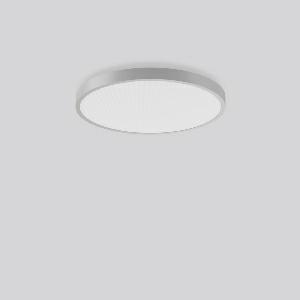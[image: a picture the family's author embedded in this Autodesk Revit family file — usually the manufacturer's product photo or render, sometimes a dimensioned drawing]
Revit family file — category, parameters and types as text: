
# Revit family: triona_round_a_312297_004_76_ec22
name_source: partatom
category: Lighting Fixtures
units: mm (PartAtom-declared; Revit-internal decimal feet)

## family parameters
Cut with Voids When Loaded = No
Host = Face
Light Source = No
Part Type = Normal
Room Calculation Point = No
Round Connector Dimension = Use Diameter
Shared = No

## types (1)
- TRIONA round A (1 x LED Modul 830, 6700 lm, 3000)
    Apparent Load = 64 VA
    CIE Flux Codes = 58 86 97 73 100
    Color Rendering = 80
    Color Temperature = 3000
    Default Elevation = 1800 mm
    Description = Series: TRIONA round
Decorative round LED surface-mounted luminaire. Flat, seamless frame: aluminium extrusion profile, powder coated. Cover made of sheet steel, powder-coated. Direct light emission through a diffuser plastic opal/prismatic. Indirect light emission through a flush diffuser made of satin-finish plastic. Lightguide and diffuser made of non-yellowing plastic (PMMA). Lateral light emission (RZB SIDELITE technology) for above-average homogeneous light distribution. Direct 70%, indirect 30% light emission. Suitable for Ceiling mounting, Wall (surface). Tool-free mounting via bayonet connection. Electronic ballast included. Very easy installation thanks to Plug+Play connection. Perfect for office areas (RUG < 19) and environments with computer screens in accordance with EN 12464-1. 
Colour: silver, matt (approx. RAL 9006)
Diameter: 681 mm
Height: 88 mm
Lamp: LED
Socket: without socket
Colour temperature: 3000K
Colour rendering index (CRI): 80
System power: 64 W
Rated luminous flux: 6700 lm
Luminous efficiency: 105 lm/W
Control gear: Converter, dimmable, DALI
Protection class: I
Type of protection: IP 20
    Height = 88 mm
    Lamp = 1 x LED Modul 830
    Lamp Light Flux = 6700 lm
    Lamp count = 1
    Length = 681 mm
    Lifetime = 50000 h
    Luminous efficacy = 105 lm/W
    Manufacturer = RZB
    ModVariant = No
    Model = 312297.004.76
    Mounting Place = Ceiling
    Mounting Type = Surface mounted
    Number of Poles = 1
    OnlyDefault = Yes
    Power Factor = 1
    Product Name = TRIONA round A
    Product group = Surface mounted modular luminaires
    ProductGroupID = 306
    Protection Class = Protection class I
    Protection Degree = IP 20
    RLX_Detail_Level = 1
    RLX_Emergency_Light_Flux = 0 lm
    RLX_Emergency_Type = 0
    RLX_Emergency_Type_DB = No
    RlxData = <blob elided: 41465 chars, md5=32bb5582>
    Socket = socket
    Standby Power = 0 W
    System Light Flux = 6700 lm
    System Power = 64 W
    Type Comments = Product without accessories
    Type Image = 312297.004.jpg
    URL = http://relux.com
    VarID = ---
    Voltage = 230 V
    Voltage Range = 220-240 V
    Weight = 0.00 kg
    Width = 0 mm  [stored 0 ft]

note: [stored X ft] marks values corroborated as IEEE doubles in the binary element streams (Revit-internal decimal feet)

## geometry (parser evidence)
native form markers: Blend x4, Sweep x14
no freeform markers — native parametric forms only
